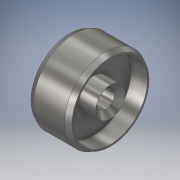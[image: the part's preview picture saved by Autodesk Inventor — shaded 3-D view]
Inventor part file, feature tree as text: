
AUTODESK INVENTOR PART (.ipt)
format: ipt  version: 2019 (Build 230136000, 136)  size: 149,504 bytes
history: native  units: mm
features: revolve x1, sketch x1
ambient origin geometry x8: Origin, YZ Plane, XZ Plane, XY Plane, X Axis, Y Axis, Z Axis, Center Point
bodies: Solid1 (feature_tree)
feature tree (2):
  revolve  "Revolution1"  [1 undecoded]
  sketch  "Sketch1"  dims[d0=50.0mm d1=18.0mm d2=38.0mm d3=11.0mm d4=39.0mm d5=27.0mm d6=2.0mm d7=2.0mm d8=10.0mm d9=20.0mm d10=90.0deg]
note: 1 required parameter value undecoded (feature->parameter linkage not recoverable at this tier; creation-order binding heuristic only, values carry confidence <= 0.55)
